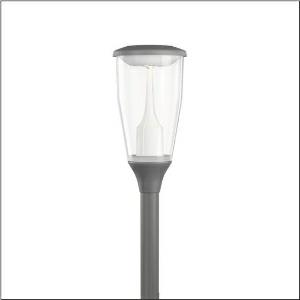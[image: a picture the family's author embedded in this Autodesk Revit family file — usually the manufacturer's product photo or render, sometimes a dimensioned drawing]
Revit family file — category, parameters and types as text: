
# Revit family: dl_11_iq___p1_0a_5xa5565lf14h000022_286d
name_source: partatom
category: Lighting Fixtures
units: mm (PartAtom-declared; Revit-internal decimal feet)

## family parameters
Cut with Voids When Loaded = No
Host = Face
Light Source = No
Part Type = Normal
Room Calculation Point = No
Round Connector Dimension = Use Diameter
Shared = No

## types (1)
- --- (1 x LED, 1530 lm, 10 W, 4000K)
    Apparent Load = 10 VA
    CIE Flux Codes = 34 63 91 95 100
    Color Rendering = 70
    Color Temperature = 4000K
    Default Elevation = 1800 mm
    Description = DL 11 iQ, mast luminaire, Module 540 iQ-SR, primary light control with 3 zone facetted reflector, of plastic, silver coated, highly specular, structured, primary optical cover: cover, of PMMA, transparent, light distribution: P1.0a, light emission: direct distribution, primary light characteristic: asymmetric, installation type: post-top, LED, High Power LED, rated luminous flux: 1.560lm, luminous efficacy: 149lm/W, light colour: 740, colour temperature: 4000K, control gear: iQ Street-Remote, control: Street-Remote, Auto-Match, Temp-Guard, Lumen-Switch, Night-Set, Smart-Wire, Light-Fading, Desk-Remote (wireless, voltage-free reading and setting of iQ features in the workshop via application-optimized NFC function/RFID function), optimised constant luminous flux control (CLO 2.0), mains connection: 220..240V, AC, 50/60Hz, connection cable pre-assembled, cable length: 5,5m, start of lifetime: 10W, end of service life: 10W, reduction: 5W, luminaire housing, upper part, of diecast aluminium, coated, Siteco® metallic grey (DB 702S), spigot size: 60mm (post-top), mounting height: 3..5m, post-top mast mounting element, of diecast aluminium, coated, Siteco® metallic grey (DB 702S), Module 540 iQ-SR, traffic white (RAL 9016), equipment: standard, protection rating (complete): IP66, insulation class (complete): insulation class II (safety insulation), certification: CE, ENEC, ENEC+, VDE, impact resistance: IK07, packaging unit: 1 piece

Light Distribution: P1.0a
    Height = 665 mm
    Lamp = 1 x LED
    Lamp Light Flux = 1530 lm
    Lamp Power = 10 W
    Lamp count = 1
    Length = 334 mm
    Luminous efficacy = 153 lm/W
    Manufacturer = Siteco
    ModVariant = No
    Model = 5XA5565LF14H000022
    Number of Poles = 1
    OnlyDefault = Yes
    Power Factor = 1
    Product Name = DL 11 iQ | P1.0a
    Product group = mast luminaire | pylon top
    ProductGroupID = 6100
    Protection Class = Protection class II
    Protection Degree = IP 66
    RLX_Detail_Level = 1
    RLX_Emergency_Light_Flux = 0 lm
    RLX_Emergency_Type = 0
    RLX_Emergency_Type_DB = No
    RlxData = <blob elided: 107861 chars, md5=b5ca5ade>
    Socket = socket
    Standby Power = 0 W
    System Light Flux = 1530 lm
    System Power = 10 W
    Type Comments = factory setting: luminous flux: 100 % | dim-lin: 254 | 401 mA
    Type Image = l_1258354.jpg
    URL = http://relux.com
    VarID = @adj_091786
    Voltage = 0 V
    Weight = 0.00 kg
    Width = 0 mm  [stored 0 ft]

note: [stored X ft] marks values corroborated as IEEE doubles in the binary element streams (Revit-internal decimal feet)

## geometry (parser evidence)
native form markers: Blend x4, Sweep x9
no freeform markers — native parametric forms only
